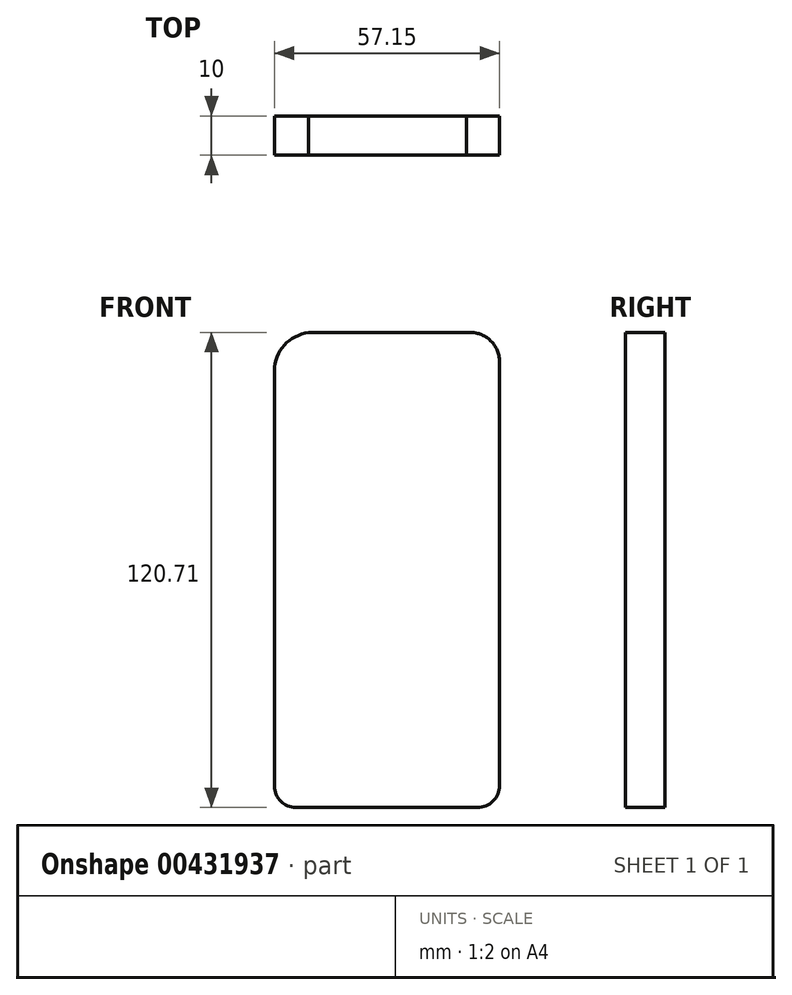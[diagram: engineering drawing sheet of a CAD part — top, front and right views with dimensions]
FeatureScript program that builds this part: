
annotation { "Feature Type Name" : "Feature", "Feature Type Description" : "" }
export const myFeature = defineFeature(function(context is Context, id is Id, definition is map)
    precondition{}
    {
        {
            var Q0;
            Q0=qCreatedBy(makeId("Front.planeOp"),FACE);
            var sketch = newSketch(context, id + "F0", { "sketchPlane" : qUnion([Q0])});
            skLineSegment(sketch, "E0", {"start": v(-45.59, 90.62) * mm, "end": v(-45.59, -14.92) * mm});
            skLineSegment(sketch, "E1", {"start": v(11.56, 92.92) * mm, "end": v(11.56, -14.72) * mm});
            skArc(sketch, "E2", {"start": v(-45.59, 90.62) * mm, "mid": v(-43.1, 97.12) * mm, "end": v(-36.92, 100.31) * mm});
            skArc(sketch, "E3", {"start": v(11.56, 92.92) * mm, "mid": v(9.03, 98.52) * mm, "end": v(3.15, 100.31) * mm});
            skArc(sketch, "E4", {"start": v(-45.59, -14.92) * mm, "mid": v(-44, -18.75) * mm, "end": v(-40.17, -20.34) * mm});
            skArc(sketch, "E5", {"start": v(11.56, -14.72) * mm, "mid": v(9.92, -18.7) * mm, "end": v(5.95, -20.34) * mm});
            skLineSegment(sketch, "E6", {"start": v(-40.17, -20.34) * mm, "end": v(5.95, -20.34) * mm});
            skLineSegment(sketch, "E7", {"start": v(-36.92, 100.31) * mm, "end": v(3.15, 100.31) * mm});
            skSolve(sketch);
        }
        {
            var Q0;
            Q0=makeQuery(id+"F0.imprint","IMPRINT",FACE,{"disambiguationData":[TD([[makeQuery(id+"F0.imprint","IMPRINT",EDGE,{"derivedFrom":sQuery(id+"F0.wireOp",EDGE,"E0")}),1.0]])]});
            extrude(context, id + "F1", {"entities" : qUnion([Q0]), "depth" : 10 * mm});
        }
    });
